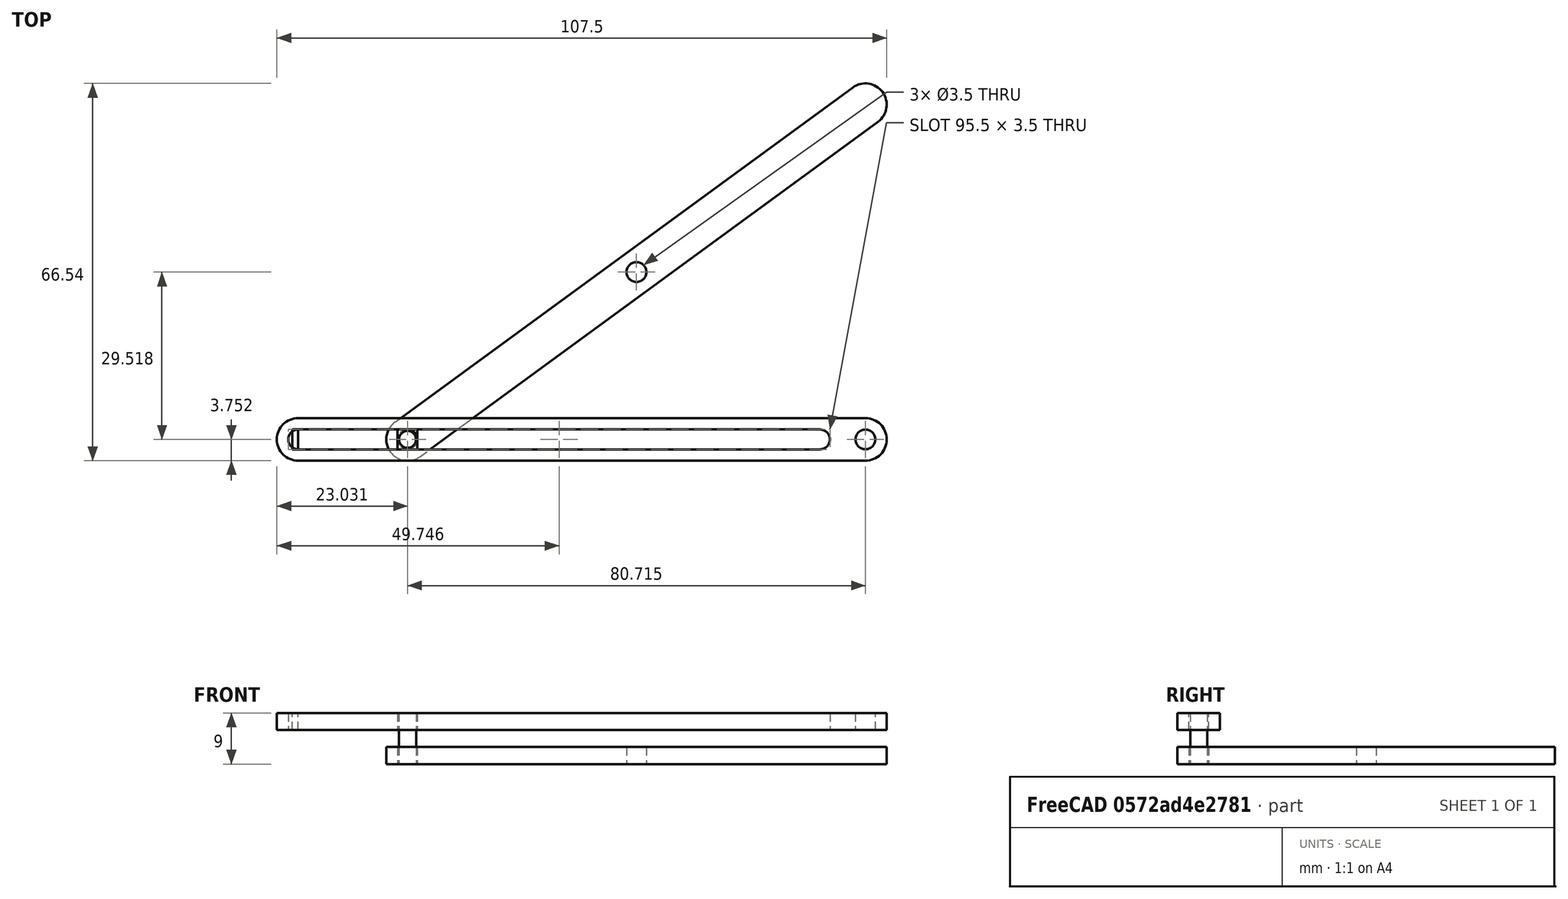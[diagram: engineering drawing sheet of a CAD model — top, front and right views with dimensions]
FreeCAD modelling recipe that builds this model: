
FCSTD DOCUMENT  (FreeCAD 0.22R38495 (Git))
Label: scissor_lift_stops
License: All rights reserved
LicenseURL: http://en.wikipedia.org/wiki/All_rights_reserved
objects: App::FeaturePython×10, PartDesign::Body×8, Sketcher::SketchObject×5, PartDesign::Pad×5, PartDesign::FeatureBase×3, PartDesign::SubShapeBinder×1, Assembly::JointGroup×1, Assembly::AssemblyObject×1
note: 40 computed .brp shape members not serialized (recipe doc carries the construction recipe); baked Part::Feature solids carry a one-line shape summary decoded from their .brp

FEATURE [Sketcher::SketchObject] Sketch
  ArcFitTolerance = 1e-06
  AttachmentSupport = -> [XZ_Plane,XY_Plane]
  FullyConstrained = true
  MakeInternals = false
  MapMode = 5
  Placement = pos=(0,0,0) rot=(1,0,0;1.5708rad)
  sketch-geometry (9):
    g0: ArcOfCircle CenterX=-50 CenterY=-4e-16 CenterZ=0 NormalX=0 NormalY=0 NormalZ=1 AngleXU=0 Radius=3.75 StartAngle=1.5708 EndAngle=4.71239
    g1: ArcOfCircle CenterX=50 CenterY=4e-16 CenterZ=0 NormalX=0 NormalY=0 NormalZ=1 AngleXU=0 Radius=3.75 StartAngle=4.71239 EndAngle=7.85398
    g2: LineSegment StartX=-50 StartY=3.75 StartZ=0 EndX=50 EndY=3.75 EndZ=0
    g3: LineSegment StartX=-50 StartY=-3.75 StartZ=0 EndX=50 EndY=-3.75 EndZ=0
    g4: ArcOfCircle CenterX=-50 CenterY=-4e-16 CenterZ=0 NormalX=0 NormalY=0 NormalZ=1 AngleXU=0 Radius=1.75 StartAngle=1.5708 EndAngle=4.71239
    g5: ArcOfCircle CenterX=42 CenterY=0 CenterZ=0 NormalX=0 NormalY=0 NormalZ=1 AngleXU=0 Radius=1.75 StartAngle=4.71239 EndAngle=7.85398
    g6: LineSegment StartX=-50 StartY=1.75 StartZ=0 EndX=42 EndY=1.75 EndZ=0
    g7: LineSegment StartX=-50 StartY=-1.75 StartZ=0 EndX=42 EndY=-1.75 EndZ=0
    g8: Circle CenterX=50 CenterY=4e-16 CenterZ=0 NormalX=0 NormalY=0 NormalZ=1 AngleXU=0 Radius=1.75
  constraints (20):
    c: Tangent(g0,g2) = 1.5708
    c: Tangent(g0,g3) = -1.5708
    c: Tangent(g1,g2) = 1.5708
    c: Tangent(g1,g3) = -1.5708
    c: Equal(g0,g1)
    c: Horizontal(g3)
    c: Tangent(g4,g6) = 1.5708
    c: Tangent(g4,g7) = -1.5708
    c: Tangent(g5,g6) = 1.5708
    c: Tangent(g5,g7) = -1.5708
    c: Equal(g4,g5)
    c: Distance(g4,g4) = 3.5
    c: Coincident(g4,g0)
    c: DistanceX(g0,g1) = 100
    c: Distance(g1,g1) = 7.5
    c: Coincident(g8,g1)
    c: Diameter(g8) = 3.5
    c: Symmetric(g0,g1,g-1)
    c: PointOnObject(g5,g-1)
    c: DistanceX(g5,g1) = 8
FEATURE [PartDesign::Pad] Pad
  Direction = (0,-1,2e-16)
  Length = 3
  Length2 = 10
  Placement = pos=(0,0,0) rot=(1,0,0;1.5708rad)
  Profile = -> Sketch
  ReferenceAxis = -> Sketch [N_Axis]
  Suppressed = false
  Type = 0
FEATURE [PartDesign::Body] Body  label="base"
  AllowCompound = false
  Group = -> [Sketch,Pad]
  Origin = -> Origin
  Placement = pos=(0.39609,-4.19756,1.45633) rot=(1,0,0;4.71239rad)
  Tip = -> Pad
FEATURE [PartDesign::SubShapeBinder] Binder
  BindCopyOnChange = 0
  BindMode = 0
  ClaimChildren = false
  Context = -> Assembly [Body001.Binder.]
  Fuse = false
  MakeFace = true
  OffsetFill = false
  OffsetIntersection = false
  OffsetJoinType = 0
  OffsetOpenResult = false
  PartialLoad = false
  Relative = true
  Support = -> [Body]
  _Version = 2
FEATURE [Sketcher::SketchObject] Sketch001
  ArcFitTolerance = 1e-06
  AttachmentSupport = -> [XY_Plane001]
  FullyConstrained = false
  MakeInternals = false
  MapMode = 5
  sketch-geometry (6):
    g0: ArcOfCircle CenterX=-50 CenterY=0 CenterZ=0 NormalX=0 NormalY=0 NormalZ=1 AngleXU=0 Radius=3.75 StartAngle=1.5708 EndAngle=4.71239
    g1: ArcOfCircle CenterX=50 CenterY=-8.2e-15 CenterZ=0 NormalX=0 NormalY=0 NormalZ=1 AngleXU=0 Radius=3.75 StartAngle=4.71239 EndAngle=7.85398
    g2: LineSegment StartX=-50 StartY=3.75 StartZ=0 EndX=50 EndY=3.75 EndZ=0
    g3: LineSegment StartX=-50 StartY=-3.75 StartZ=0 EndX=50 EndY=-3.75 EndZ=0
    g4: Circle CenterX=0 CenterY=0 CenterZ=0 NormalX=0 NormalY=0 NormalZ=1 AngleXU=0 Radius=1.75
    g5: Circle CenterX=-50 CenterY=0 CenterZ=0 NormalX=0 NormalY=0 NormalZ=1 AngleXU=0 Radius=1.75
  constraints (9):
    c: Tangent(g0,g2) = 1.5708
    c: Tangent(g0,g3) = -1.5708
    c: Tangent(g1,g2) = 1.5708
    c: Tangent(g1,g3) = -1.5708
    c: Equal(g0,g1)
    c: Horizontal(g3)
    c: Symmetric(g0,g1,g-1)
    c: Coincident(g4,g-1)
    c: Coincident(g5,g0)
FEATURE [PartDesign::Pad] Pad001
  Direction = (0,0,1)
  Length = 3
  Length2 = 10
  Profile = -> Sketch001
  ReferenceAxis = -> Sketch001 [N_Axis]
  Suppressed = false
  Type = 0
FEATURE [PartDesign::Body] Body001  label="arm_1"
  AllowCompound = false
  Group = -> [Binder,Sketch001,Pad001]
  Origin = -> Origin001
  Placement = pos=(10.0387,25.32,-1.54367) rot=(0,0,1;2.5101rad)
  Tip = -> Pad001
FEATURE [PartDesign::FeatureBase] Clone
  BaseFeature = -> Body001
  Placement = pos=(0,18.3,0) rot=(0,0,1;0rad)
  Suppressed = false
FEATURE [PartDesign::Body] Body002  label="arm_2"
  AllowCompound = false
  Group = -> [Clone]
  Origin = -> Origin002
  Placement = pos=(20.8422,10.5492,-4.54367) rot=(0,0,1;0.631493rad)
  Tip = -> Clone
FEATURE [Sketcher::SketchObject] Sketch002
  ArcFitTolerance = 1e-06
  AttachmentSupport = -> [XY_Plane003]
  FullyConstrained = true
  MakeInternals = false
  MapMode = 5
  sketch-geometry (1):
    g0: Circle CenterX=0 CenterY=0 CenterZ=0 NormalX=0 NormalY=0 NormalZ=1 AngleXU=0 Radius=1.5
  constraints (2):
    c: Coincident(g0,g-1)
    c: Diameter(g0) = 3
FEATURE [PartDesign::Pad] Pad002
  Direction = (0,0,1)
  Length = 9
  Length2 = 10
  Profile = -> Sketch002
  ReferenceAxis = -> Sketch002 [N_Axis]
  Suppressed = false
  Type = 0
FEATURE [PartDesign::Body] Body003  label="pin_1"
  AllowCompound = false
  Group = -> [Sketch002,Pad002]
  Origin = -> Origin003
  Placement = pos=(50.3961,-4.19756,4.45633) rot=(1,0,0;3.14159rad)
  Tip = -> Pad002
FEATURE [PartDesign::FeatureBase] Clone001
  BaseFeature = -> Body003
  Placement = pos=(-22.5,-16.7,0) rot=(0,0,1;0rad)
  Suppressed = false
FEATURE [PartDesign::Body] Body004  label="pin_2"
  AllowCompound = false
  Group = -> [Clone001]
  Origin = -> Origin004
  Placement = pos=(32.6906,8.82653,-6.04367) rot=(0,0,-1;1.26786rad)
  Tip = -> Clone001
FEATURE [PartDesign::FeatureBase] Clone002
  BaseFeature = -> Body004
  Suppressed = false
FEATURE [PartDesign::Body] Body005  label="pin_3"
  AllowCompound = false
  Group = -> [Clone002]
  Origin = -> Origin005
  Placement = pos=(-14.6097,19.0053,-4.54367) rot=(0,0,1;0.337153rad)
  Tip = -> Clone002
FEATURE [App::FeaturePython] GroundedJoint  # Assembly grounded joint (typed FeaturePython)
  ObjectToGround = -> Body
  Placement = pos=(0.39609,-4.19756,1.45633) rot=(1,0,0;4.71239rad)
FEATURE [Sketcher::SketchObject] Sketch003
  ArcFitTolerance = 1e-06
  AttachmentSupport = -> [XY_Plane007]
  FullyConstrained = true
  MakeInternals = false
  MapMode = 5
  sketch-geometry (4):
    g0: LineSegment StartX=-1.75 StartY=1.75 StartZ=0 EndX=-1.75 EndY=-1.75 EndZ=0
    g1: LineSegment StartX=-1.75 StartY=-1.75 StartZ=0 EndX=1.75 EndY=-1.75 EndZ=0
    g2: LineSegment StartX=1.75 StartY=-1.75 StartZ=0 EndX=1.75 EndY=1.75 EndZ=0
    g3: LineSegment StartX=1.75 StartY=1.75 StartZ=0 EndX=-1.75 EndY=1.75 EndZ=0
  constraints (11):
    c: Coincident(g0,g1)
    c: Coincident(g1,g2)
    c: Coincident(g2,g3)
    c: Coincident(g3,g0)
    c: Vertical(g0)
    c: Vertical(g2)
    c: Horizontal(g1)
    c: Horizontal(g3)
    c: DistanceY(g0,g0) = 3.5
    c: Equal(g3,g0)
    c: Symmetric(g0,g1,g-1)
FEATURE [PartDesign::Pad] Pad003
  Direction = (0,0,1)
  Length = 3
  Length2 = 10
  Profile = -> Sketch003
  ReferenceAxis = -> Sketch003 [N_Axis]
  Suppressed = false
  Type = 0
FEATURE [PartDesign::Body] Body006  label="pin_slider"
  AllowCompound = false
  Group = -> [Sketch003,Pad003]
  Origin = -> Origin007
  Placement = pos=(-30.3186,-4.19756,4.45633) rot=(-0.707107,0.707107,0;3.14159rad)
  Tip = -> Pad003
FEATURE [Sketcher::SketchObject] Sketch004
  ArcFitTolerance = 1e-06
  AttachmentSupport = -> [XY_Plane008]
  FullyConstrained = true
  MakeInternals = false
  MapMode = 5
  sketch-geometry (4):
    g0: LineSegment StartX=-1 StartY=1.75 StartZ=0 EndX=-1 EndY=-1.75 EndZ=0
    g1: LineSegment StartX=-1 StartY=-1.75 StartZ=0 EndX=0 EndY=-1.75 EndZ=0
    g2: LineSegment StartX=0 StartY=-1.75 StartZ=0 EndX=0 EndY=1.75 EndZ=0
    g3: LineSegment StartX=0 StartY=1.75 StartZ=0 EndX=-1 EndY=1.75 EndZ=0
  constraints (11):
    c: Coincident(g1,g2)
    c: Coincident(g2,g3)
    c: Coincident(g3,g0)
    c: Vertical(g0)
    c: Vertical(g2)
    c: Horizontal(g1)
    c: Horizontal(g3)
    c: Distance(g0,g0) = 3.5
    c: DistanceX(g3,g3) = 1
    c: Coincident(g0,g1)
    c: Symmetric(g2,g1,g-1)
FEATURE [PartDesign::Pad] Pad004
  Direction = (0,0,1)
  Length = 3
  Length2 = 10
  Profile = -> Sketch004
  ReferenceAxis = -> Sketch004 [N_Axis]
  Suppressed = false
  Type = 0
FEATURE [PartDesign::Body] Body007  label="pin_stop"
  AllowCompound = false
  Group = -> [Sketch004,Pad004]
  Origin = -> Origin008
  Placement = pos=(-49.6039,-4.19756,1.45633) rot=(0,0,1;0rad)
  Tip = -> Pad004
FEATURE [App::FeaturePython] Revolute  # Assembly joint (typed FeaturePython)
  Activated = true
  AngleMax = 0
  AngleMin = 0
  Detach1 = false
  Detach2 = false
  Distance = 0
  Distance2 = 0
  EnableAngleMax = false
  EnableAngleMin = false
  EnableLengthMax = false
  EnableLengthMin = false
  JointType = 1 (Revolute)
  LengthMax = 0
  LengthMin = 0
  Offset = (0,0,0)
  Placement2 = pos=(50,-3,0) rot=(-1,0,0;4.71239rad)
  Reference1 = -> Assembly [Body003.Pad002.Edge2,Body003.Pad002.Edge2]
  Reference2 = -> Assembly [Body.Pad.Edge27,Body.Pad.Edge27]
  Rotation = 0
FEATURE [App::FeaturePython] Cylindrical  # Assembly joint (typed FeaturePython)
  Activated = true
  AngleMax = 0
  AngleMin = 0
  Detach1 = false
  Detach2 = false
  Distance = 0
  Distance2 = 0
  EnableAngleMax = false
  EnableAngleMin = false
  EnableLengthMax = false
  EnableLengthMin = false
  JointType = 2 (Cylindrical)
  LengthMax = 0
  LengthMin = 0
  Offset = (0,0,0)
  Placement1 = pos=(0,0,9) rot=(0,0,1;0rad)
  Placement2 = pos=(-50,-3.6e-15,1.5) rot=(0,0,1;0rad)
  Reference1 = -> Assembly [Body003.Pad002.Face1,Body003.Pad002.Edge3]
  Reference2 = -> Assembly [Body001.Pad001.Face5,Body001.Pad001.Face5]
  Rotation = 0
FEATURE [App::FeaturePython] Distance  # Assembly joint (typed FeaturePython)
  Activated = true
  AngleMax = 0
  AngleMin = 0
  Detach1 = false
  Detach2 = false
  Distance = 0
  Distance2 = 0
  EnableAngleMax = false
  EnableAngleMin = false
  EnableLengthMax = false
  EnableLengthMin = false
  JointType = 5 (Distance)
  LengthMax = 0
  LengthMin = 0
  Offset = (0,0,0)
  Placement1 = pos=(0.620769,-7.1e-15,3) rot=(0,0,1;0rad)
  Placement2 = pos=(1.86655,0,1.15e-14) rot=(-0.57735,-0.57735,-0.57735;2.0944rad)
  Reference1 = -> Assembly [Body001.Pad001.Face8,Body001.Pad001.Vertex10]
  Reference2 = -> Assembly [Body.Pad.Face10,Body.Pad.Vertex15]
  Rotation = 0
FEATURE [App::FeaturePython] Revolute001  # Assembly joint (typed FeaturePython)
  Activated = true
  AngleMax = 0
  AngleMin = 0
  Detach1 = false
  Detach2 = false
  Distance = 0
  Distance2 = 0
  EnableAngleMax = false
  EnableAngleMin = false
  EnableLengthMax = false
  EnableLengthMin = false
  JointType = 1 (Revolute)
  LengthMax = 0
  LengthMin = 0
  Offset = (0,0,0)
  Placement1 = pos=(-22.5,-16.7,4.5) rot=(0,0,1;0rad)
  Reference1 = -> Assembly [Body004.Clone001.Face1,Body004.Clone001.Face1]
  Reference2 = -> Assembly [Body001.Pad001.Edge17,Body001.Pad001.Edge17]
  Rotation = 0
FEATURE [App::FeaturePython] Revolute002  # Assembly joint (typed FeaturePython)
  Activated = true
  AngleMax = 0
  AngleMin = 0
  Detach1 = false
  Detach2 = false
  Distance = 0
  Distance2 = 0
  EnableAngleMax = false
  EnableAngleMin = false
  EnableLengthMax = false
  EnableLengthMin = false
  JointType = 1 (Revolute)
  LengthMax = 0
  LengthMin = 0
  Offset = (0,0,0)
  Placement1 = pos=(-22.5,-16.7,4.5) rot=(0,0,1;0rad)
  Placement2 = pos=(0,18.3,3) rot=(0,0,1;0rad)
  Reference1 = -> Assembly [Body004.Clone001.Face1,Body004.Clone001.Face1]
  Reference2 = -> Assembly [Body002.Clone.Edge18,Body002.Clone.Edge18]
  Rotation = 0
FEATURE [App::FeaturePython] Revolute003  # Assembly joint (typed FeaturePython)
  Activated = true
  AngleMax = 0
  AngleMin = 0
  Detach1 = false
  Detach2 = false
  Distance = 0
  Distance2 = 0
  EnableAngleMax = false
  EnableAngleMin = false
  EnableLengthMax = false
  EnableLengthMin = false
  JointType = 1 (Revolute)
  LengthMax = 0
  LengthMin = 0
  Offset = (0,0,0)
  Placement1 = pos=(-22.5,-16.7,0) rot=(0,0,1;0rad)
  Placement2 = pos=(-50,18.3,0) rot=(0,0,1;0rad)
  Reference1 = -> Assembly [Body005.Clone002.Edge2,Body005.Clone002.Edge2]
  Reference2 = -> Assembly [Body002.Clone.Edge14,Body002.Clone.Edge14]
  Rotation = 0
FEATURE [App::FeaturePython] Fixed  # Assembly joint (typed FeaturePython)
  Activated = true
  AngleMax = 0
  AngleMin = 0
  Detach1 = false
  Detach2 = false
  Distance = 0
  Distance2 = 0
  EnableAngleMax = false
  EnableAngleMin = false
  EnableLengthMax = false
  EnableLengthMin = false
  JointType = 0 (Fixed)
  LengthMax = 0
  LengthMin = 0
  Offset = (0,0,0)
  Placement1 = pos=(0,1.75,1.5) rot=(0,0,1;0rad)
  Placement2 = pos=(-50,-1.5,1.75) rot=(-1,0,0;4.71239rad)
  Reference1 = -> Assembly [Body007.Pad004.Edge8,Body007.Pad004.Edge8]
  Reference2 = -> Assembly [Body.Pad.Edge13,Body.Pad.Edge13]
  Rotation = 90
FEATURE [App::FeaturePython] Slider  # Assembly joint (typed FeaturePython)
  Activated = true
  AngleMax = 0
  AngleMin = 0
  Detach1 = false
  Detach2 = false
  Distance = 0
  Distance2 = 0
  EnableAngleMax = false
  EnableAngleMin = false
  EnableLengthMax = true
  EnableLengthMin = true
  JointType = 3 (Slider)
  LengthMax = 1
  LengthMin = -90
  Offset = (0,0,0)
  Placement1 = pos=(-9e-16,1.75,1.5) rot=(0,-0.707107,0.707107;3.14159rad)
  Placement2 = pos=(0,0,1.5) rot=(-0.57735,-0.57735,0.57735;2.0944rad)
  Reference1 = -> Assembly [Body006.Pad003.Face4,Body006.Pad003.Face4]
  Reference2 = -> Assembly [Body007.Pad004.Face3,Body007.Pad004.Face3]
  Rotation = 0
FEATURE [App::FeaturePython] Revolute004  # Assembly joint (typed FeaturePython)
  Activated = true
  AngleMax = 0
  AngleMin = 0
  Detach1 = false
  Detach2 = false
  Distance = 0
  Distance2 = 0
  EnableAngleMax = false
  EnableAngleMin = false
  EnableLengthMax = false
  EnableLengthMin = false
  JointType = 1 (Revolute)
  LengthMax = 0
  LengthMin = 0
  Offset = (0,0,0)
  Placement1 = pos=(-22.5,-16.7,9) rot=(0,0,1;0rad)
  Reference1 = -> Assembly [Body005.Clone002.Edge3,Body005.Clone002.Edge3]
  Reference2 = -> Assembly [Body006.Pad003.Face5,Body006.Pad003.Face5]
  Rotation = 0
FEATURE [Assembly::JointGroup] Joints
  Group = -> [GroundedJoint,Revolute,Cylindrical,Distance,Revolute001,Revolute002,Revolute003,Fixed,Slider,Revolute004]
FEATURE [Assembly::AssemblyObject] Assembly
  Group = -> [Joints,Body,Body001,Body002,Body003,Body004,Body005,GroundedJoint,Body006,Body007,Revolute,Cylindrical,Distance,Revolute001,Revolute002,Revolute003,Fixed,Slider,Revolute004]
  Origin = -> Origin006
  Type = Assembly
